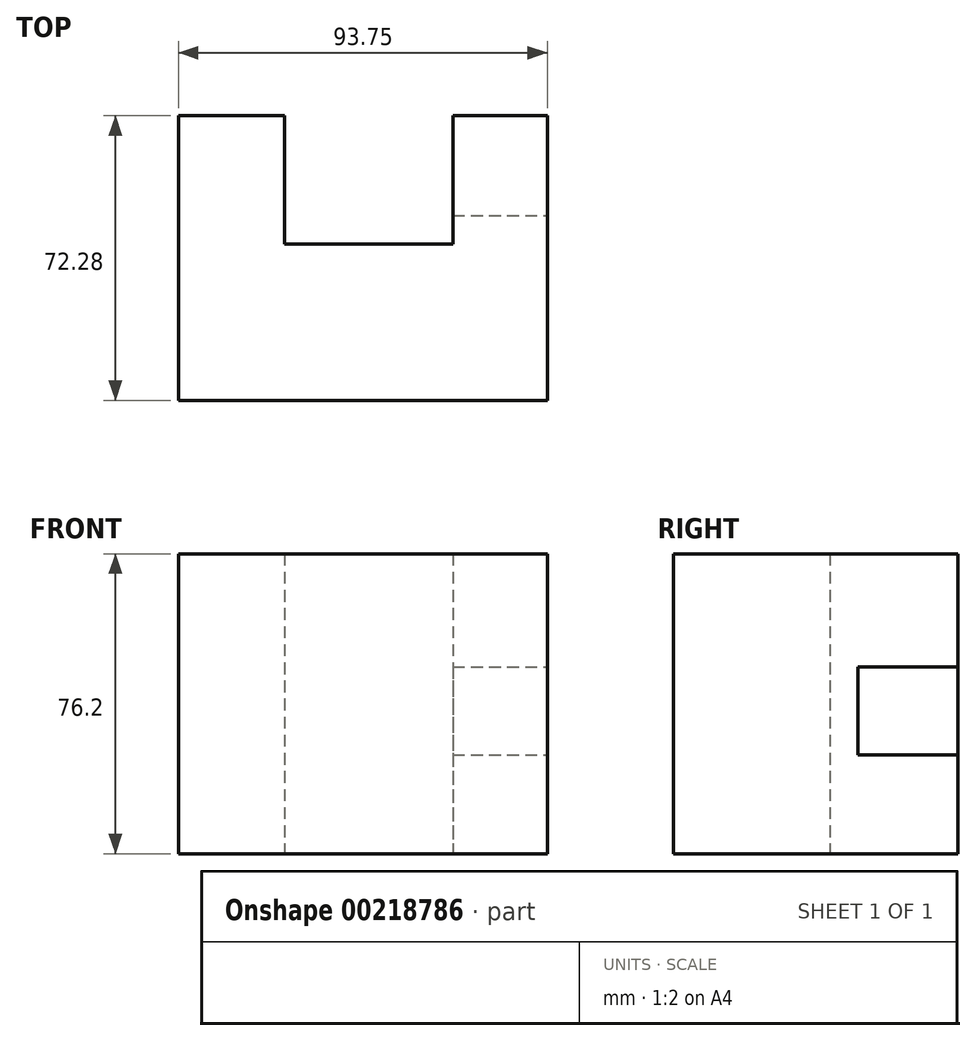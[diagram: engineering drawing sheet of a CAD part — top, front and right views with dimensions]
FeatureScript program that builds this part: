
annotation { "Feature Type Name" : "Feature", "Feature Type Description" : "" }
export const myFeature = defineFeature(function(context is Context, id is Id, definition is map)
    precondition{}
    {
        {
            var Q0;
            Q0=qCreatedBy(makeId("Top.planeOp"),FACE);
            var sketch = newSketch(context, id + "F0", { "sketchPlane" : qUnion([Q0])});
            skLineSegment(sketch, "E0.bottom", {"start": v(-45.03, 35.9) * mm, "end": v(-18.01, 35.9) * mm});
            skLineSegment(sketch, "E0.top", {"start": v(-45.03, -36.37) * mm, "end": v(48.72, -36.37) * mm});
            skLineSegment(sketch, "E0.left", {"start": v(-45.03, 35.9) * mm, "end": v(-45.03, -36.37) * mm});
            skLineSegment(sketch, "E0.right", {"start": v(48.72, 35.9) * mm, "end": v(48.72, -36.37) * mm});
            skLineSegment(sketch, "E1.top", {"start": v(-18.01, 3.35) * mm, "end": v(24.7, 3.35) * mm});
            skLineSegment(sketch, "E1.left", {"start": v(-18.01, 35.9) * mm, "end": v(-18.01, 3.35) * mm});
            skLineSegment(sketch, "E1.right", {"start": v(24.7, 35.9) * mm, "end": v(24.7, 3.35) * mm});
            skLineSegment(sketch, "E2.trimOffspring", {"start": v(24.7, 35.9) * mm, "end": v(48.72, 35.9) * mm});
            skSolve(sketch);
        }
        {
            var Q0;
            Q0=makeQuery(id+"F0.imprint","IMPRINT",FACE,{"disambiguationData":[TD([[makeQuery(id+"F0.imprint","IMPRINT",EDGE,{"derivedFrom":sQuery(id+"F0.wireOp",EDGE,"E0.bottom")}),-1.0]])]});
            extrude(context, id + "F1", {"entities" : qUnion([Q0]), "depth" : 76.2 * mm});
        }
        {
            var Q0;
            Q0=makeQuery(id+"F1.opExtrude","SWEPT_FACE",FACE,{"disambiguationData":[OSD([sQuery(id+"F0.wireOp",EDGE,"E2.trimOffspring")])]});
            var sketch = newSketch(context, id + "F2", { "sketchPlane" : qUnion([Q0])});
            skLineSegment(sketch, "E3.bottom", {"start": v(-24.7, 25.06) * mm, "end": v(-48.72, 25.06) * mm});
            skLineSegment(sketch, "E3.top", {"start": v(-24.7, 47.45) * mm, "end": v(-48.72, 47.45) * mm});
            skLineSegment(sketch, "E3.left", {"start": v(-24.7, 25.06) * mm, "end": v(-24.7, 47.45) * mm});
            skLineSegment(sketch, "E3.right", {"start": v(-48.72, 25.06) * mm, "end": v(-48.72, 47.45) * mm});
            skSolve(sketch);
        }
        {
            var Q0;
            Q0=makeQuery(id+"F2.imprint","IMPRINT",FACE,{"disambiguationData":[TD([[makeQuery(id+"F2.imprint","IMPRINT",EDGE,{"derivedFrom":sQuery(id+"F2.wireOp",EDGE,"E3.bottom")}),-1.0]])]});
            extrude(context, id + "F3", {"entities" : qUnion([Q0]), "operationType" : NewBodyOperationType.REMOVE, "oppositeDirection" : true, "depth" : 25.4 * mm});
        }
    });
